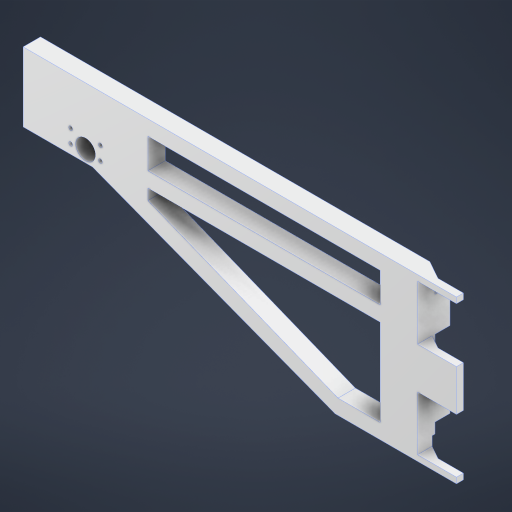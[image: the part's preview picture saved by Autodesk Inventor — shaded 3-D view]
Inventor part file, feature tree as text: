
AUTODESK INVENTOR PART (.ipt)
format: ipt  version: 2024 (Build 280153000, 153)  size: 442,880 bytes
history: native  units: mm
features: sketch x13, extrude x11, other x1, fillet x1
ambient origin geometry x8: Origin, YZ Plane, XZ Plane, XY Plane, X Axis, Y Axis, Z Axis, Center Point
bodies: Body1 (feature_tree)
feature tree (26):
  other  "Твердое тело1"
  extrude  "Выдавливание1"  Depth=10.0mm
  extrude  "Выдавливание2"  Depth=650.0mm
  sketch  "Эскиз3"
  sketch  "Эскиз4"
  sketch  "Эскиз5"
  extrude  "Выдавливание3"  Depth=280.0mm TaperAngle=0.0deg
  extrude  "Выдавливание4"  Depth=120.0mm
  fillet  "Сопряжение1"  Radius=120.0mm
  extrude  "Выдавливание5"  Depth=55.0mm TaperAngle=0.0deg
  extrude  "Extrusion13"  Depth=3.0mm
  sketch  "Sketch16"  dims[d2=650.0mm d3=650.0mm]
  extrude  "Extrusion14"  Depth=100.0mm TaperAngle=0.0deg
  extrude  "Extrusion15"  Depth=26.0mm
  extrude  "Extrusion16"  Depth=26.0mm
  extrude  "Extrusion17"  Depth=20.0mm TaperAngle=0.0deg
  extrude  "Extrusion18"  TaperAngle=0.0deg  [1 undecoded]
  sketch  "Эскиз1"
  sketch  "Эскиз2"
  sketch  "Эскиз6"
  sketch  "Sketch14"  dims[d0=20.0mm d1=10.0mm]
  sketch  "Sketch17"  dims[d4=0.0mm d5=280.0mm d6=0.0mm]
  sketch  "Sketch18"  dims[d7=99.0mm d8=0.0mm d9=120.0mm d10=120.0mm]
  sketch  "Sketch19"  dims[d11=4.25mm d12=4.25mm d13=4.25mm d14=4.25mm d15=19.0mm d16=34.0mm]
  sketch  "Sketch20"  dims[d17=4.25mm d18=4.25mm d19=4.25mm d20=4.25mm d21=19.0mm d22=34.0mm d23=55.0mm d24=0.0mm]
  sketch  "Sketch21"  dims[d25=5.0mm d26=0.0mm d27=3.0mm d28=100.0mm d29=0.0mm d54=26.0mm d55=26.0mm d56=20.0mm d57=0.0mm d58=0.0mm d59=100.0mm d60=0.0mm d61=26.344949mm d64=10.0mm d65=10.0mm d66=30.0mm d67=0.0mm d68=73.0mm d69=52.0mm d70=52.0mm d71=1000.0mm d72=0.0mm d73=78.0mm d74=78.0mm d75=0.0mm d76=0.0mm d77=19.0mm d79=94.0mm d80=50.0mm d81=10.0mm d82=0.0mm d83=55.0mm d84=55.0mm d85=60.0mm d86=60.0mm d87=26.0mm d88=0.0mm]
note: 1 required parameter value undecoded (feature->parameter linkage not recoverable at this tier; creation-order binding heuristic only, values carry confidence <= 0.55)
